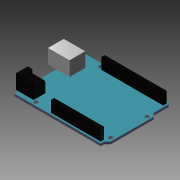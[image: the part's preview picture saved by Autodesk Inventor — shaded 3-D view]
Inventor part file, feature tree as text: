
AUTODESK INVENTOR PART (.ipt)
format: ipt  version: 2015 (Build 190159000, 159)  size: 184,832 bytes
history: native  units: mm
features: extrude x8, sketch x8, other x1, fillet x1
ambient origin geometry x8: Origin, YZ Plane, XZ Plane, XY Plane, X Axis, Y Axis, Z Axis, Center Point
bodies: Body1 (feature_tree)
feature tree (18):
  other  "ソリッド1"
  extrude  "基板"  Depth=66.04mm
  extrude  "取付穴"  Depth=2.54mm
  extrude  "電源ジャック"  Depth=2.54mm
  extrude  "押し出し4"  Depth=2.54mm
  extrude  "押し出し5"  Depth=32.766mm
  fillet  "フィレット1"  Radius=2.54mm
  extrude  "USBジャック"  Depth=2.54mm
  extrude  "POWER ANALOG IN"  Depth=11.43mm
  extrude  "DIGITAL"  Depth=1.524mm
  sketch  "スケッチ1"
  sketch  "スケッチ2"
  sketch  "スケッチ4"
  sketch  "スケッチ5"
  sketch  "スケッチ6"
  sketch  "スケッチ7"
  sketch  "スケッチ8"
  sketch  "スケッチ9"
